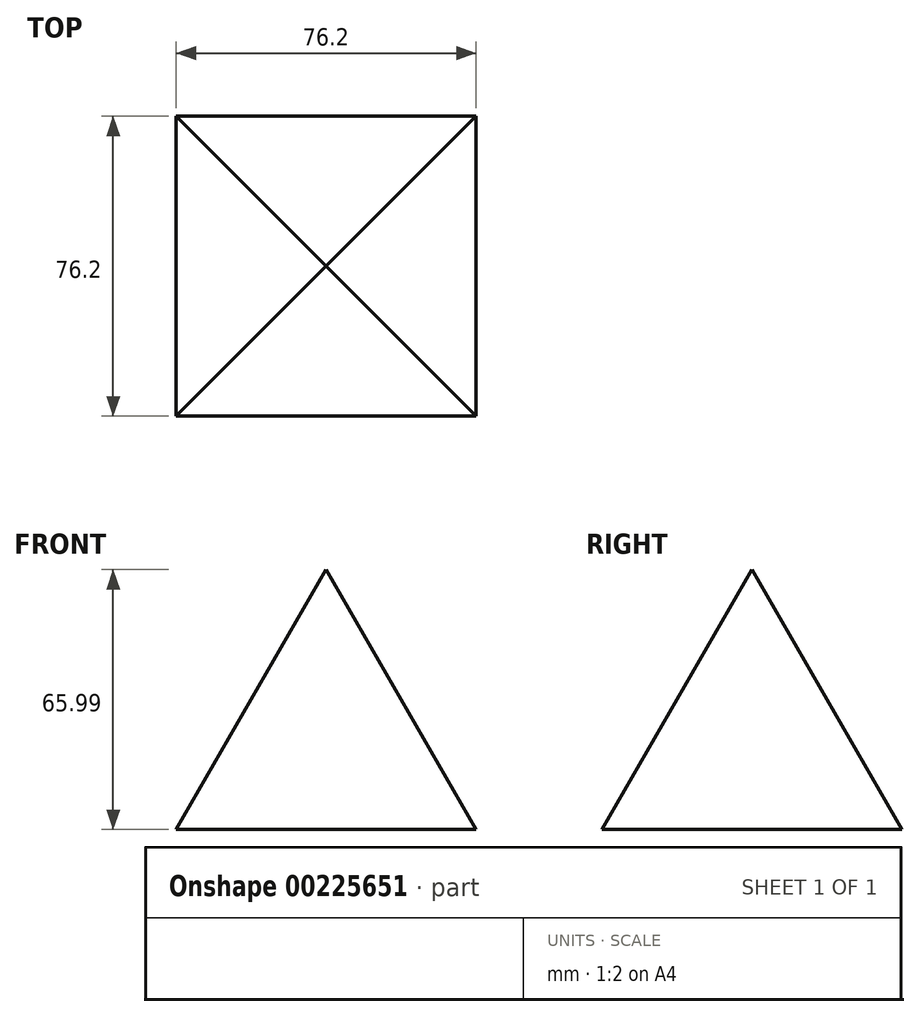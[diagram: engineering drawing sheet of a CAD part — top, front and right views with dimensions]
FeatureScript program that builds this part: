
annotation { "Feature Type Name" : "Feature", "Feature Type Description" : "" }
export const myFeature = defineFeature(function(context is Context, id is Id, definition is map)
    precondition{}
    {
        {
            var Q0;
            Q0=qCreatedBy(makeId("Top.planeOp"),FACE);
            var sketch = newSketch(context, id + "F0", { "sketchPlane" : qUnion([Q0])});
            skLineSegment(sketch, "E0.bottom", {"start": v(-32.36, 47.28) * mm, "end": v(43.84, 47.28) * mm});
            skLineSegment(sketch, "E0.top", {"start": v(-32.36, -28.92) * mm, "end": v(43.84, -28.92) * mm});
            skLineSegment(sketch, "E0.left", {"start": v(-32.36, 47.28) * mm, "end": v(-32.36, -28.92) * mm});
            skLineSegment(sketch, "E0.right", {"start": v(43.84, 47.28) * mm, "end": v(43.84, -28.92) * mm});
            skSolve(sketch);
        }
        {
            var Q0;
            Q0 = qSketchRegion(id + "F0", true);
            extrude(context, id + "F1", {"entities" : qUnion([Q0]), "depth" : 76.2 * mm, "hasDraft" : true, "draftAngle" : 30 * degree, "draftPullDirection" : true});
        }
    });
